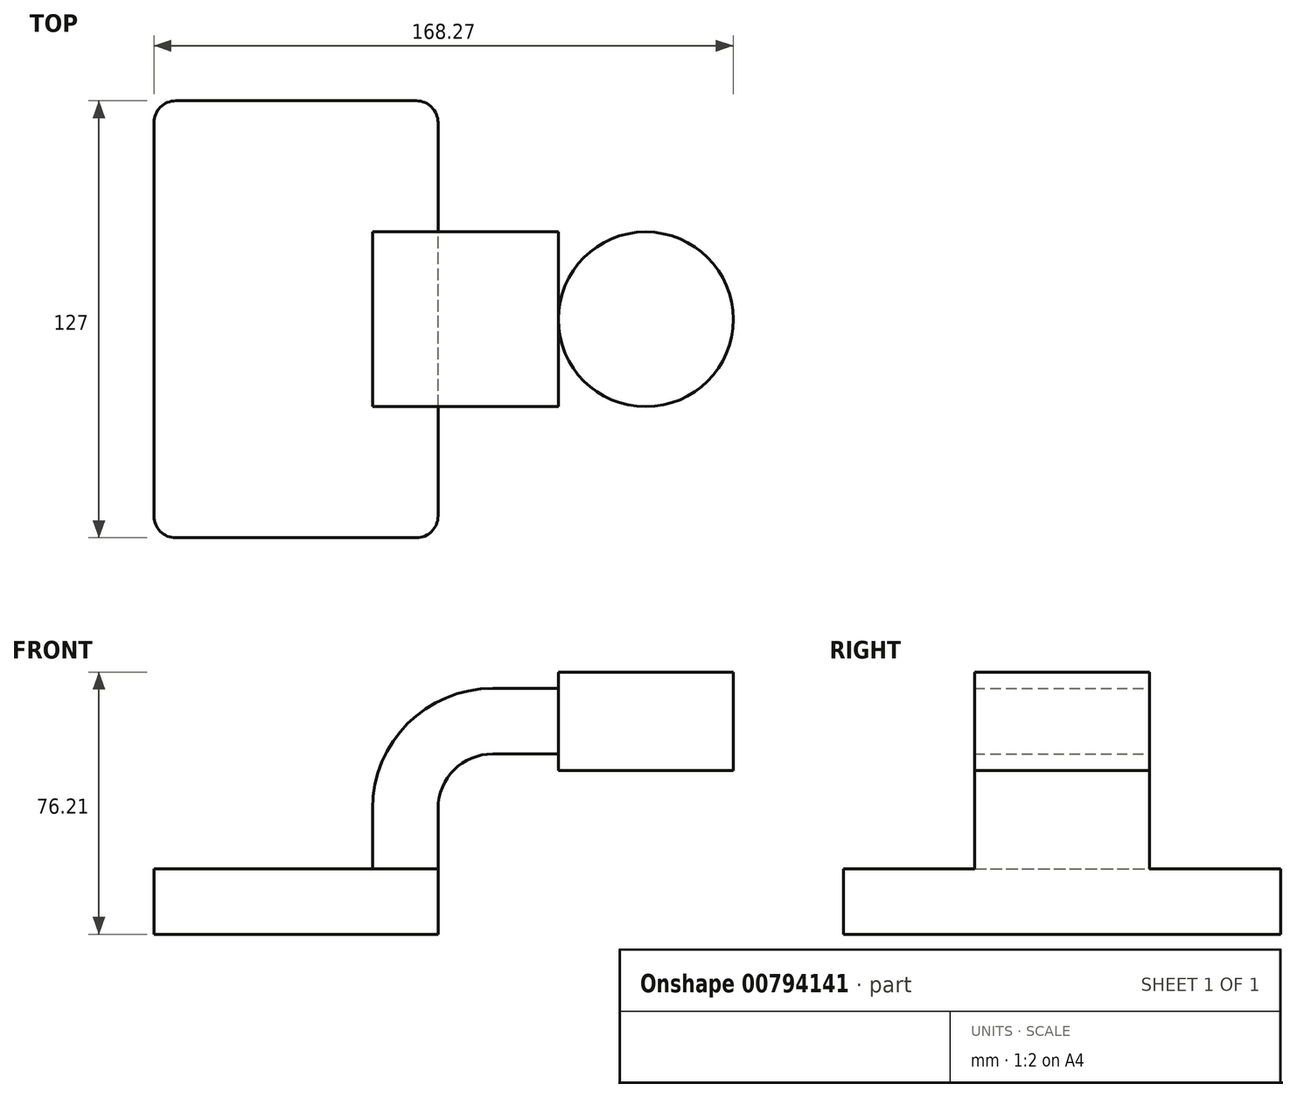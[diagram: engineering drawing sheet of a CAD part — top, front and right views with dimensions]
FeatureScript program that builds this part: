
annotation { "Feature Type Name" : "Feature", "Feature Type Description" : "" }
export const myFeature = defineFeature(function(context is Context, id is Id, definition is map)
    precondition{}
    {
        {
            var Q0;
            Q0=qCreatedBy(makeId("Front.planeOp"),FACE);
            var sketch = newSketch(context, id + "F0", { "sketchPlane" : qUnion([Q0])});
            skLineSegment(sketch, "E0.bottom", {"start": v(-41.28, 9.52) * mm, "end": v(41.27, 9.53) * mm});
            skLineSegment(sketch, "E0.top", {"start": v(-41.28, -9.53) * mm, "end": v(41.28, -9.53) * mm});
            skLineSegment(sketch, "E0.left", {"start": v(-41.28, 9.52) * mm, "end": v(-41.28, -9.53) * mm});
            skLineSegment(sketch, "E0.right", {"start": v(41.27, 9.53) * mm, "end": v(41.28, -9.52) * mm});
            skPoint(sketch, "E0.middle", {"position": v(0, 0) * mm});
            skLineSegment(sketch, "E1.bottom", {"start": v(76.2, 66.67) * mm, "end": v(127, 66.67) * mm});
            skLineSegment(sketch, "E1.top", {"start": v(76.2, 38.1) * mm, "end": v(127, 38.1) * mm});
            skLineSegment(sketch, "E1.left", {"start": v(76.2, 66.67) * mm, "end": v(76.2, 38.1) * mm});
            skLineSegment(sketch, "E1.right", {"start": v(127, 66.67) * mm, "end": v(127, 38.1) * mm});
            skPoint(sketch, "E1.middle", {"position": v(101.6, 52.39) * mm});
            skLineSegment(sketch, "E2", {"start": v(41.27, 9.53) * mm, "end": v(41.27, 27) * mm});
            skArc(sketch, "E3", {"start": v(41.27, 27) * mm, "mid": v(45.92, 38.23) * mm, "end": v(57.15, 42.88) * mm});
            skLineSegment(sketch, "E4", {"start": v(57.15, 42.88) * mm, "end": v(101.6, 42.88) * mm});
            skLineSegment(sketch, "E5.0", {"start": v(57.15, 61.93) * mm, "end": v(101.6, 61.93) * mm});
            skArc(sketch, "E5.1", {"start": v(22.22, 27) * mm, "mid": v(32.45, 51.7) * mm, "end": v(57.15, 61.93) * mm});
            skLineSegment(sketch, "E5.2", {"start": v(22.23, 9.53) * mm, "end": v(22.23, 27) * mm});
            skLineSegment(sketch, "E6", {"start": v(101.6, 38.1) * mm, "end": v(101.6, 66.67) * mm});
            skFitSpline(sketch, "E7", {"points": [v(-41.28, 9.53) * mm, v(76.2, 61.93) * mm], "startDerivative": vector(-3.26, 44.05) * mm, "endDerivative": vector(216.04, -12.93) * mm});
            skSolve(sketch);
        }
        {
            var Q0;
            Q0=makeQuery(id+"F0.imprint","IMPRINT",FACE,{"disambiguationData":[TD([[makeQuery(id+"F0.imprint","IMPRINT",EDGE,{"derivedFrom":sQuery(id+"F0.wireOp",EDGE,"E0.top")}),1.0]])]});
            extrude(context, id + "F1", {"entities" : qUnion([Q0]), "endBound" : BoundingType.SYMMETRIC, "depth" : 127 * mm, "offsetDistance" : 25.4 * mm});
        }
        {
            var Q0;
            {var subQ1=sQuery(id+"F0.wireOp",EDGE,"E2");Q0=makeQuery(id+"F0.imprint","IMPRINT",FACE,{"disambiguationData":[TD([[makeQuery(id+"F0.imprint","IMPRINT",EDGE,{"derivedFrom":subQ1}),1.0]])]});}
            extrude(context, id + "F2", {"entities" : qUnion([Q0]), "operationType" : NewBodyOperationType.ADD, "endBound" : BoundingType.SYMMETRIC, "depth" : 50.8 * mm, "offsetDistance" : 25.4 * mm});
        }
        {
            var Q0;
            {var subQ0=sQuery(id+"F0.wireOp",EDGE,"E5.1");Q0=makeQuery(id+"F0.imprint","IMPRINT",FACE,{"disambiguationData":[TD([[makeQuery(id+"F0.imprint","IMPRINT",EDGE,{"derivedFrom":subQ0}),1.0]])]});}
            extrude(context, id + "F3", {"entities" : qUnion([Q0]), "operationType" : NewBodyOperationType.ADD, "endBound" : BoundingType.SYMMETRIC, "depth" : 15.88 * mm, "offsetDistance" : 25.4 * mm});
        }
        {
            var Q0;
            {var subQ0=sQuery(id+"F0.wireOp",EDGE,"E1.right");Q0=makeQuery(id+"F0.imprint","IMPRINT",FACE,{"disambiguationData":[TD([[makeQuery(id+"F0.imprint","IMPRINT",EDGE,{"derivedFrom":subQ0}),-1.0]])]});}
            var Q1;
            Q1=sQuery(id+"F0.wireOp",EDGE,"E6");
            revolve(context, id + "F4", {"operationType" : NewBodyOperationType.ADD, "surfaceOperationType" : NewSurfaceOperationType.NEW, "entities" : qUnion([Q0]), "axis" : qUnion([Q1]), "revolveType" : RevolveType.FULL});
        }
        {
            var Q0;
            Q0=makeQuery(id+"F1.opExtrude","CAP_EDGE",EDGE,{"disambiguationData":[OSD([sQuery(id+"F0.wireOp",EDGE,"E0.right")])],"isStart":false});
            var Q1;
            Q1=makeQuery(id+"F1.opExtrude","CAP_EDGE",EDGE,{"disambiguationData":[OSD([sQuery(id+"F0.wireOp",EDGE,"E0.left")])],"isStart":false});
            var Q2;
            Q2=makeQuery(id+"F1.opExtrude","CAP_EDGE",EDGE,{"disambiguationData":[OSD([sQuery(id+"F0.wireOp",EDGE,"E0.left")])],"isStart":true});
            var Q3;
            Q3=makeQuery(id+"F1.opExtrude","CAP_EDGE",EDGE,{"disambiguationData":[OSD([sQuery(id+"F0.wireOp",EDGE,"E0.right")])],"isStart":true});
            fillet(context, id + "F5", {"entities" : qUnion([Q0, Q1, Q2, Q3]), "radius" : 6.35 * mm, "tangentPropagation" : true, "allowEdgeOverflow" : false});
        }
    });
